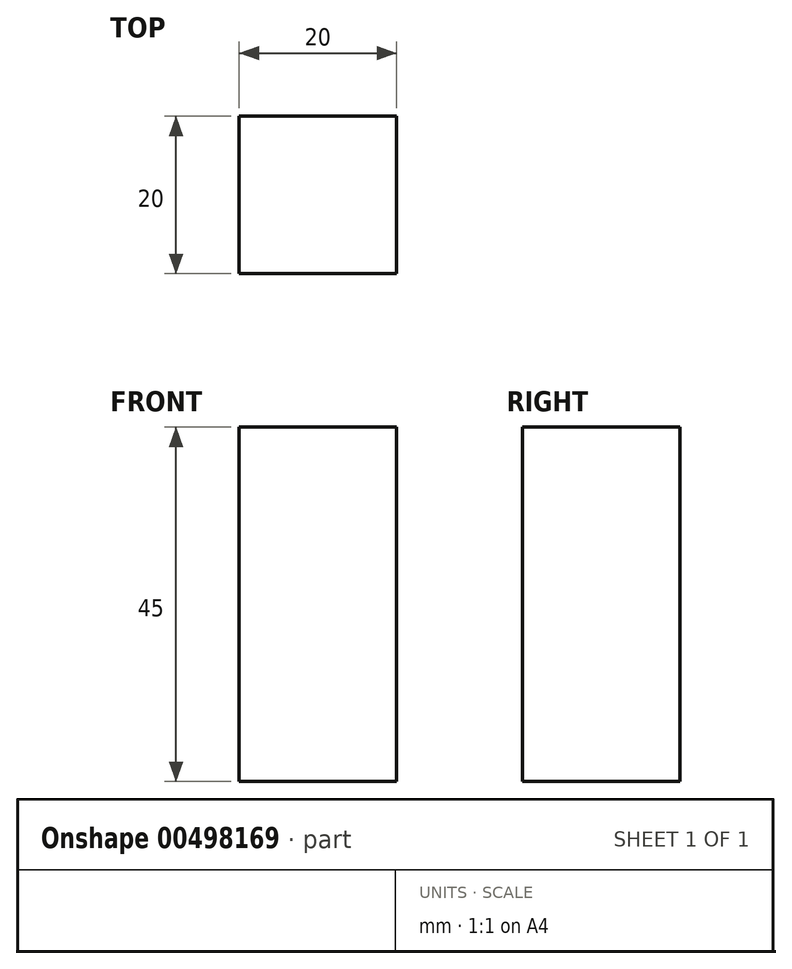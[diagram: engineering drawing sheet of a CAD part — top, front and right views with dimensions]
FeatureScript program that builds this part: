
annotation { "Feature Type Name" : "Feature", "Feature Type Description" : "" }
export const myFeature = defineFeature(function(context is Context, id is Id, definition is map)
    precondition{}
    {
        {
            var Q0;
            Q0=qCreatedBy(makeId("Front.planeOp"),FACE);
            var sketch = newSketch(context, id + "F0", { "sketchPlane" : qUnion([Q0])});
            skLineSegment(sketch, "E0.bottom", {"start": v(10, 22.5) * mm, "end": v(-10, 22.5) * mm});
            skLineSegment(sketch, "E0.top", {"start": v(10, -22.5) * mm, "end": v(-10, -22.5) * mm});
            skLineSegment(sketch, "E0.left", {"start": v(10, 22.5) * mm, "end": v(10, -22.5) * mm});
            skLineSegment(sketch, "E0.right", {"start": v(-10, 22.5) * mm, "end": v(-10, -22.5) * mm});
            skPoint(sketch, "E0.middle", {"position": v(0, 0) * mm});
            skSolve(sketch);
        }
        {
            var Q0;
            Q0 = qSketchRegion(id + "F0", true);
            extrude(context, id + "F1", {"entities" : qUnion([Q0]), "depth" : 20 * mm});
        }
    });
